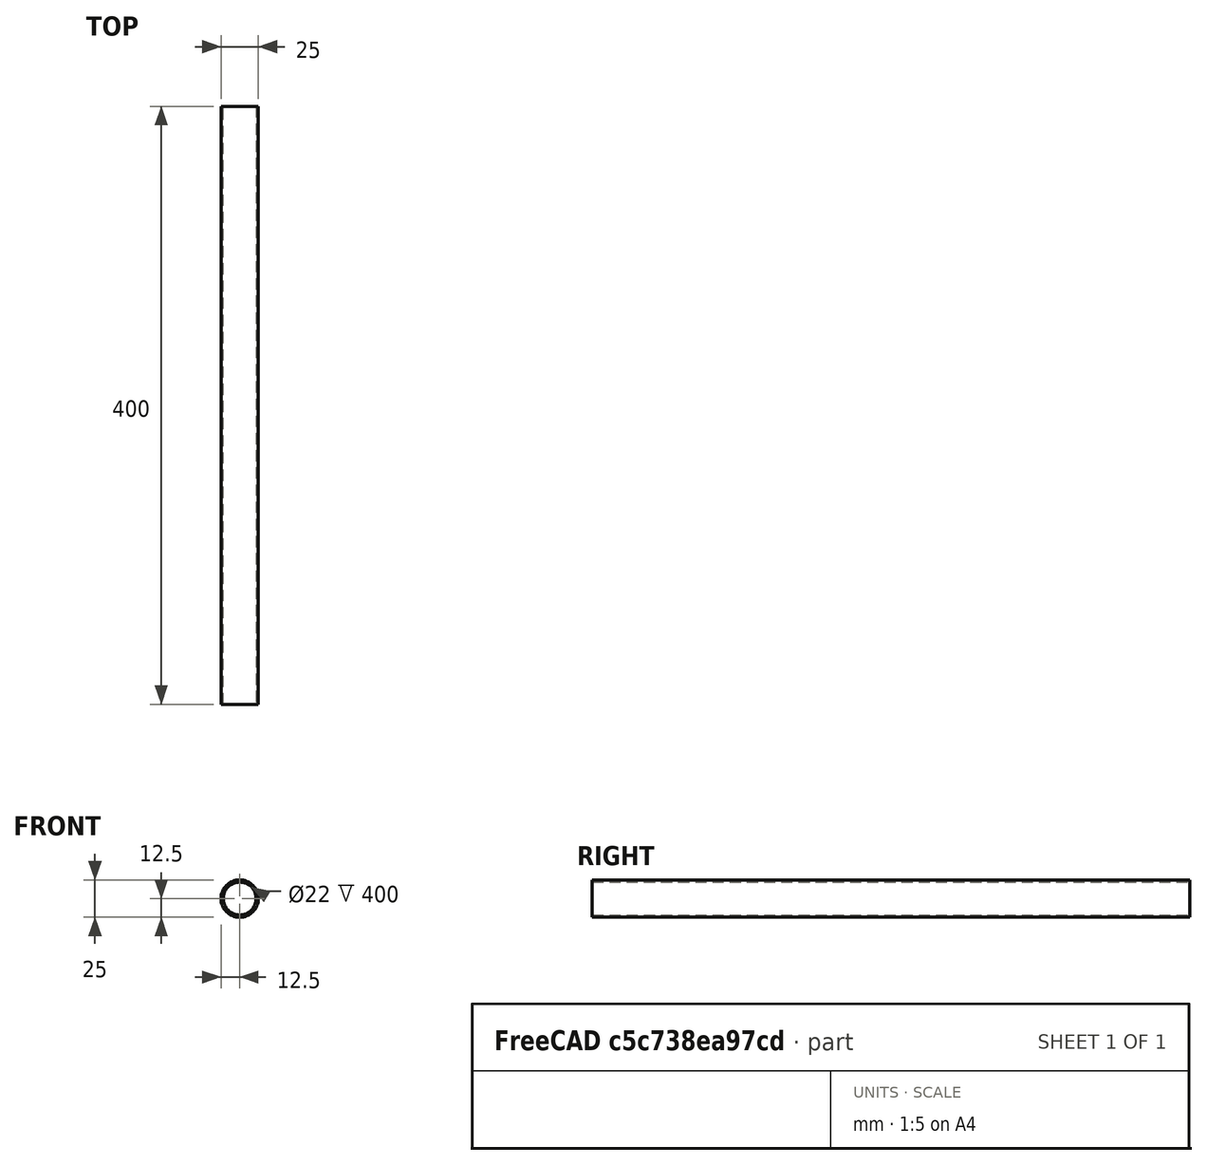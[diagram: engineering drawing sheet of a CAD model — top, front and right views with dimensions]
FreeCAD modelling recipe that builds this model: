
FCSTD DOCUMENT  (FreeCAD 0.21R32110 (Git))
Label: Yoke Column
License: All rights reserved
LicenseURL: http://en.wikipedia.org/wiki/All_rights_reserved
objects: Sketcher::SketchObject×1, PartDesign::Pad×1, App::Part×1
note: 3 computed .brp shape members not serialized (recipe doc carries the construction recipe); baked Part::Feature solids carry a one-line shape summary decoded from their .brp

FEATURE [Sketcher::SketchObject] Sketch004
  AttachmentOffset = pos=(0,0,-120) rot=(0,0,1;0rad)
  FullyConstrained = true
  MapMode = 5
  Placement = pos=(0,148,0) rot=(1,0,0;1.5708rad)
  sketch-geometry (2):
    g0: Circle CenterX=0 CenterY=0 CenterZ=0 NormalX=0 NormalY=0 NormalZ=1 AngleXU=0 Radius=12.5
    g1: Circle CenterX=0 CenterY=0 CenterZ=0 NormalX=0 NormalY=0 NormalZ=1 AngleXU=0 Radius=11
  constraints (4):
    c: Coincident(g0,g-1)
    c: Diameter(g0) = 25
    c: Coincident(g1,g0)
    c: Diameter(g1) = 22
FEATURE [PartDesign::Pad] Pad004  label="Yoke Tube 25mm Dia"
  Direction = (0,-1,0)
  Length = 400
  Length2 = 10
  Placement = pos=(0,148,0) rot=(1,0,0;1.5708rad)
  Profile = -> Sketch004
  ReferenceAxis = -> Sketch004 [N_Axis]
  Type = 0
FEATURE [App::Part] Part
  Group = -> [Sketch004,Pad004]
  Origin = -> Origin
